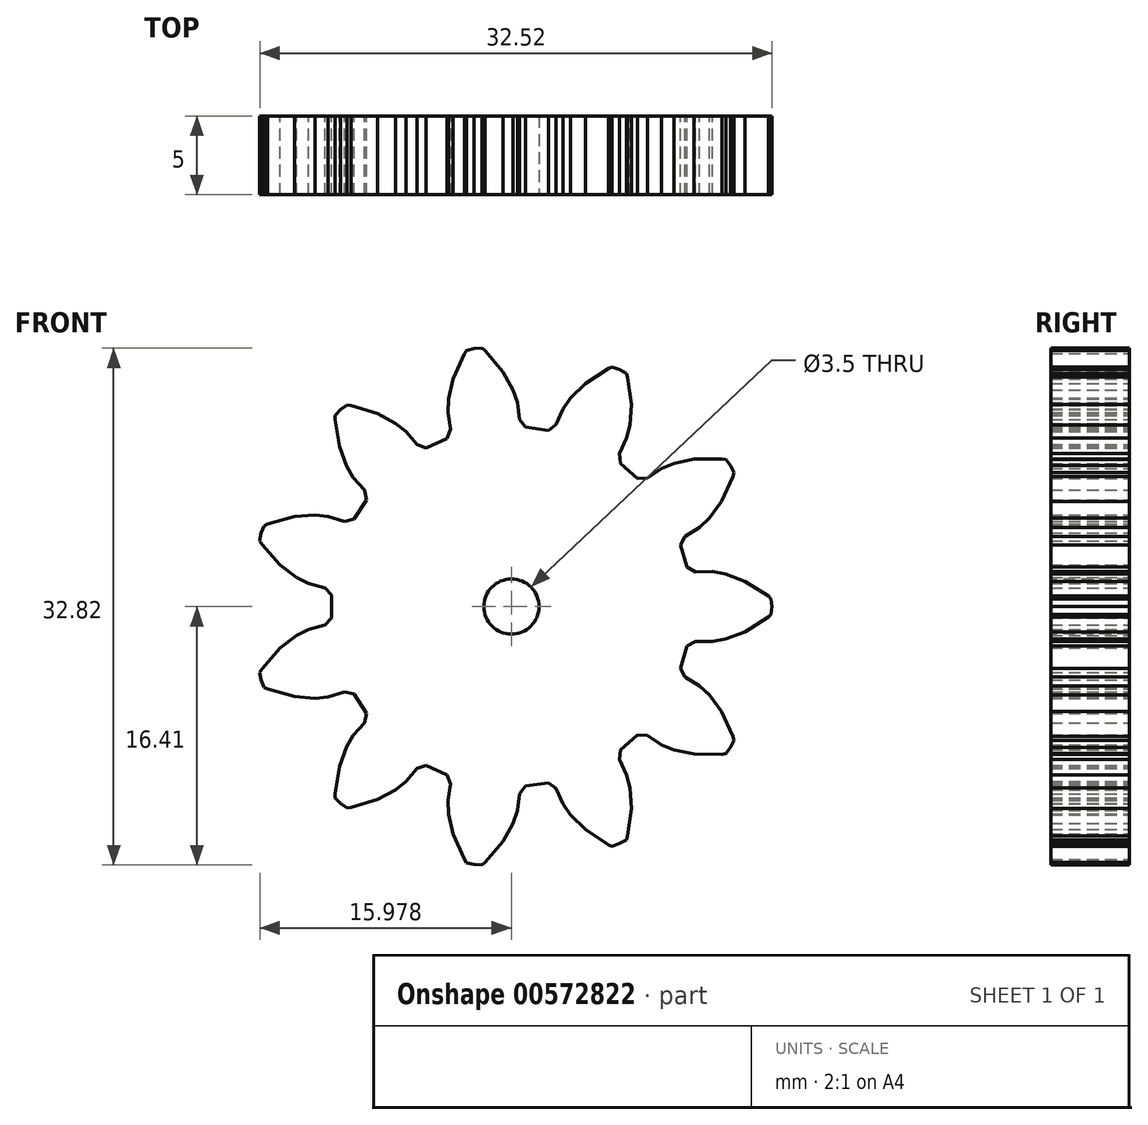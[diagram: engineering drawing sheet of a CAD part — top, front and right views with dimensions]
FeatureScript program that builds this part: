
annotation { "Feature Type Name" : "Feature", "Feature Type Description" : "" }
export const myFeature = defineFeature(function(context is Context, id is Id, definition is map)
    precondition{}
    {
        {
            var Q0;
            Q0=qCreatedBy(makeId("Front.planeOp"),FACE);
            var sketch = newSketch(context, id + "F0", { "sketchPlane" : qUnion([Q0])});
            skLineSegment(sketch, "E0", {"start": v(-15.98, 5.13) * mm, "end": v(-16.17, 4.66) * mm});
            skLineSegment(sketch, "E1", {"start": v(-16.17, 4.66) * mm, "end": v(-16.26, 4.17) * mm});
            skLineSegment(sketch, "E2", {"start": v(-16.26, 4.17) * mm, "end": v(-16.14, 3.96) * mm});
            skLineSegment(sketch, "E3", {"start": v(-16.14, 3.96) * mm, "end": v(-14.97, 2.64) * mm});
            skLineSegment(sketch, "E4", {"start": v(-14.97, 2.64) * mm, "end": v(-13.93, 1.85) * mm});
            skLineSegment(sketch, "E5", {"start": v(-13.93, 1.85) * mm, "end": v(-13.17, 1.47) * mm});
            skLineSegment(sketch, "E6", {"start": v(-13.17, 1.47) * mm, "end": v(-12.13, 1.18) * mm});
            skLineSegment(sketch, "E7", {"start": v(-12.13, 1.18) * mm, "end": v(-11.7, 0.73) * mm});
            skLineSegment(sketch, "E8", {"start": v(-11.7, 0.73) * mm, "end": v(-11.7, -0.73) * mm});
            skLineSegment(sketch, "E9", {"start": v(-11.7, -0.73) * mm, "end": v(-12.13, -1.18) * mm});
            skLineSegment(sketch, "E10", {"start": v(-12.13, -1.18) * mm, "end": v(-13.17, -1.47) * mm});
            skLineSegment(sketch, "E11", {"start": v(-13.17, -1.47) * mm, "end": v(-13.93, -1.85) * mm});
            skLineSegment(sketch, "E12", {"start": v(-13.93, -1.85) * mm, "end": v(-14.97, -2.64) * mm});
            skLineSegment(sketch, "E13", {"start": v(-14.97, -2.64) * mm, "end": v(-16.14, -3.96) * mm});
            skLineSegment(sketch, "E14", {"start": v(-16.14, -3.96) * mm, "end": v(-16.26, -4.17) * mm});
            skLineSegment(sketch, "E15", {"start": v(-16.26, -4.17) * mm, "end": v(-16.17, -4.66) * mm});
            skLineSegment(sketch, "E16", {"start": v(-16.17, -4.66) * mm, "end": v(-15.98, -5.13) * mm});
            skLineSegment(sketch, "E17", {"start": v(-15.98, -5.13) * mm, "end": v(-15.76, -5.24) * mm});
            skLineSegment(sketch, "E18", {"start": v(-15.76, -5.24) * mm, "end": v(-14.06, -5.71) * mm});
            skLineSegment(sketch, "E19", {"start": v(-14.06, -5.71) * mm, "end": v(-12.76, -5.82) * mm});
            skLineSegment(sketch, "E20", {"start": v(-12.76, -5.82) * mm, "end": v(-11.92, -5.73) * mm});
            skLineSegment(sketch, "E21", {"start": v(-11.92, -5.73) * mm, "end": v(-10.89, -5.41) * mm});
            skLineSegment(sketch, "E22", {"start": v(-10.89, -5.41) * mm, "end": v(-10.28, -5.55) * mm});
            skLineSegment(sketch, "E23", {"start": v(-10.28, -5.55) * mm, "end": v(-9.5, -6.78) * mm});
            skLineSegment(sketch, "E24", {"start": v(-9.5, -6.78) * mm, "end": v(-9.62, -7.4) * mm});
            skLineSegment(sketch, "E25", {"start": v(-9.62, -7.4) * mm, "end": v(-10.33, -8.2) * mm});
            skLineSegment(sketch, "E26", {"start": v(-10.33, -8.2) * mm, "end": v(-10.77, -8.93) * mm});
            skLineSegment(sketch, "E27", {"start": v(-10.77, -8.93) * mm, "end": v(-11.2, -10.16) * mm});
            skLineSegment(sketch, "E28", {"start": v(-11.2, -10.16) * mm, "end": v(-11.48, -11.9) * mm});
            skLineSegment(sketch, "E29", {"start": v(-11.48, -11.9) * mm, "end": v(-11.47, -12.15) * mm});
            skLineSegment(sketch, "E30", {"start": v(-11.47, -12.15) * mm, "end": v(-11.13, -12.5) * mm});
            skLineSegment(sketch, "E31", {"start": v(-11.13, -12.5) * mm, "end": v(-10.72, -12.8) * mm});
            skLineSegment(sketch, "E32", {"start": v(-10.72, -12.8) * mm, "end": v(-10.47, -12.77) * mm});
            skLineSegment(sketch, "E33", {"start": v(-10.47, -12.77) * mm, "end": v(-8.79, -12.25) * mm});
            skLineSegment(sketch, "E34", {"start": v(-8.79, -12.25) * mm, "end": v(-7.64, -11.64) * mm});
            skLineSegment(sketch, "E35", {"start": v(-7.64, -11.64) * mm, "end": v(-6.97, -11.1) * mm});
            skLineSegment(sketch, "E36", {"start": v(-6.97, -11.1) * mm, "end": v(-6.28, -10.29) * mm});
            skLineSegment(sketch, "E37", {"start": v(-6.28, -10.29) * mm, "end": v(-5.7, -10.07) * mm});
            skLineSegment(sketch, "E38", {"start": v(-5.7, -10.07) * mm, "end": v(-4.36, -10.68) * mm});
            skLineSegment(sketch, "E39", {"start": v(-4.36, -10.68) * mm, "end": v(-4.14, -11.26) * mm});
            skLineSegment(sketch, "E40", {"start": v(-4.14, -11.26) * mm, "end": v(-4.3, -12.33) * mm});
            skLineSegment(sketch, "E41", {"start": v(-4.3, -12.33) * mm, "end": v(-4.28, -13.18) * mm});
            skLineSegment(sketch, "E42", {"start": v(-4.28, -13.18) * mm, "end": v(-3.98, -14.45) * mm});
            skLineSegment(sketch, "E43", {"start": v(-3.98, -14.45) * mm, "end": v(-3.27, -16.06) * mm});
            skLineSegment(sketch, "E44", {"start": v(-3.27, -16.06) * mm, "end": v(-3.13, -16.27) * mm});
            skLineSegment(sketch, "E45", {"start": v(-3.13, -16.27) * mm, "end": v(-2.64, -16.38) * mm});
            skLineSegment(sketch, "E46", {"start": v(-2.64, -16.38) * mm, "end": v(-2.15, -16.4) * mm});
            skLineSegment(sketch, "E47", {"start": v(-2.15, -16.4) * mm, "end": v(-1.95, -16.25) * mm});
            skLineSegment(sketch, "E48", {"start": v(-1.95, -16.25) * mm, "end": v(-0.81, -14.9) * mm});
            skLineSegment(sketch, "E49", {"start": v(-0.81, -14.9) * mm, "end": v(-0.17, -13.77) * mm});
            skLineSegment(sketch, "E50", {"start": v(-0.17, -13.77) * mm, "end": v(0.1, -12.96) * mm});
            skLineSegment(sketch, "E51", {"start": v(0.1, -12.96) * mm, "end": v(0.23, -11.9) * mm});
            skLineSegment(sketch, "E52", {"start": v(0.23, -11.9) * mm, "end": v(0.61, -11.4) * mm});
            skLineSegment(sketch, "E53", {"start": v(0.61, -11.4) * mm, "end": v(2.06, -11.19) * mm});
            skLineSegment(sketch, "E54", {"start": v(2.06, -11.19) * mm, "end": v(2.56, -11.56) * mm});
            skLineSegment(sketch, "E55", {"start": v(2.56, -11.56) * mm, "end": v(3, -12.54) * mm});
            skLineSegment(sketch, "E56", {"start": v(3, -12.54) * mm, "end": v(3.48, -13.24) * mm});
            skLineSegment(sketch, "E57", {"start": v(3.48, -13.24) * mm, "end": v(4.41, -14.15) * mm});
            skLineSegment(sketch, "E58", {"start": v(4.41, -14.15) * mm, "end": v(5.88, -15.12) * mm});
            skLineSegment(sketch, "E59", {"start": v(5.88, -15.12) * mm, "end": v(6.12, -15.22) * mm});
            skLineSegment(sketch, "E60", {"start": v(6.12, -15.22) * mm, "end": v(6.59, -15.06) * mm});
            skLineSegment(sketch, "E61", {"start": v(6.59, -15.06) * mm, "end": v(7.02, -14.8) * mm});
            skLineSegment(sketch, "E62", {"start": v(7.02, -14.8) * mm, "end": v(7.1, -14.57) * mm});
            skLineSegment(sketch, "E63", {"start": v(7.1, -14.57) * mm, "end": v(7.33, -12.82) * mm});
            skLineSegment(sketch, "E64", {"start": v(7.33, -12.82) * mm, "end": v(7.25, -11.52) * mm});
            skLineSegment(sketch, "E65", {"start": v(7.25, -11.52) * mm, "end": v(7.04, -10.7) * mm});
            skLineSegment(sketch, "E66", {"start": v(7.04, -10.7) * mm, "end": v(6.58, -9.72) * mm});
            skLineSegment(sketch, "E67", {"start": v(6.58, -9.72) * mm, "end": v(6.63, -9.1) * mm});
            skLineSegment(sketch, "E68", {"start": v(6.63, -9.1) * mm, "end": v(7.74, -8.14) * mm});
            skLineSegment(sketch, "E69", {"start": v(7.74, -8.14) * mm, "end": v(8.36, -8.18) * mm});
            skLineSegment(sketch, "E70", {"start": v(8.36, -8.18) * mm, "end": v(9.26, -8.77) * mm});
            skLineSegment(sketch, "E71", {"start": v(9.26, -8.77) * mm, "end": v(10.04, -9.1) * mm});
            skLineSegment(sketch, "E72", {"start": v(10.04, -9.1) * mm, "end": v(11.32, -9.36) * mm});
            skLineSegment(sketch, "E73", {"start": v(11.32, -9.36) * mm, "end": v(13.08, -9.38) * mm});
            skLineSegment(sketch, "E74", {"start": v(13.08, -9.38) * mm, "end": v(13.33, -9.34) * mm});
            skLineSegment(sketch, "E75", {"start": v(13.33, -9.34) * mm, "end": v(13.64, -8.95) * mm});
            skLineSegment(sketch, "E76", {"start": v(13.64, -8.95) * mm, "end": v(13.86, -8.5) * mm});
            skLineSegment(sketch, "E77", {"start": v(13.86, -8.5) * mm, "end": v(13.8, -8.26) * mm});
            skLineSegment(sketch, "E78", {"start": v(13.8, -8.26) * mm, "end": v(13.05, -6.67) * mm});
            skLineSegment(sketch, "E79", {"start": v(13.05, -6.67) * mm, "end": v(12.28, -5.62) * mm});
            skLineSegment(sketch, "E80", {"start": v(12.28, -5.62) * mm, "end": v(11.66, -5.04) * mm});
            skLineSegment(sketch, "E81", {"start": v(11.66, -5.04) * mm, "end": v(10.75, -4.47) * mm});
            skLineSegment(sketch, "E82", {"start": v(10.75, -4.47) * mm, "end": v(10.45, -3.92) * mm});
            skLineSegment(sketch, "E83", {"start": v(10.45, -3.92) * mm, "end": v(10.86, -2.51) * mm});
            skLineSegment(sketch, "E84", {"start": v(10.86, -2.51) * mm, "end": v(11.4, -2.2) * mm});
            skLineSegment(sketch, "E85", {"start": v(11.4, -2.2) * mm, "end": v(12.49, -2.22) * mm});
            skLineSegment(sketch, "E86", {"start": v(12.49, -2.22) * mm, "end": v(13.32, -2.07) * mm});
            skLineSegment(sketch, "E87", {"start": v(13.32, -2.07) * mm, "end": v(14.54, -1.6) * mm});
            skLineSegment(sketch, "E88", {"start": v(14.54, -1.6) * mm, "end": v(16.03, -0.67) * mm});
            skLineSegment(sketch, "E89", {"start": v(16.03, -0.67) * mm, "end": v(16.22, -0.5) * mm});
            skLineSegment(sketch, "E90", {"start": v(16.22, -0.5) * mm, "end": v(16.26, 0) * mm});
            skLineSegment(sketch, "E91", {"start": v(16.26, 0) * mm, "end": v(16.22, 0.5) * mm});
            skLineSegment(sketch, "E92", {"start": v(16.22, 0.5) * mm, "end": v(16.03, 0.67) * mm});
            skLineSegment(sketch, "E93", {"start": v(16.03, 0.67) * mm, "end": v(14.54, 1.6) * mm});
            skLineSegment(sketch, "E94", {"start": v(14.54, 1.6) * mm, "end": v(13.32, 2.07) * mm});
            skLineSegment(sketch, "E95", {"start": v(13.32, 2.07) * mm, "end": v(12.49, 2.22) * mm});
            skLineSegment(sketch, "E96", {"start": v(12.49, 2.22) * mm, "end": v(11.4, 2.2) * mm});
            skLineSegment(sketch, "E97", {"start": v(11.4, 2.2) * mm, "end": v(10.86, 2.51) * mm});
            skLineSegment(sketch, "E98", {"start": v(10.86, 2.51) * mm, "end": v(10.45, 3.92) * mm});
            skLineSegment(sketch, "E99", {"start": v(10.45, 3.92) * mm, "end": v(10.75, 4.47) * mm});
            skLineSegment(sketch, "E100", {"start": v(10.75, 4.47) * mm, "end": v(11.66, 5.04) * mm});
            skLineSegment(sketch, "E101", {"start": v(11.66, 5.04) * mm, "end": v(12.28, 5.62) * mm});
            skLineSegment(sketch, "E102", {"start": v(12.28, 5.62) * mm, "end": v(13.05, 6.67) * mm});
            skLineSegment(sketch, "E103", {"start": v(13.05, 6.67) * mm, "end": v(13.8, 8.26) * mm});
            skLineSegment(sketch, "E104", {"start": v(13.8, 8.26) * mm, "end": v(13.86, 8.5) * mm});
            skLineSegment(sketch, "E105", {"start": v(13.86, 8.5) * mm, "end": v(13.64, 8.95) * mm});
            skLineSegment(sketch, "E106", {"start": v(13.64, 8.95) * mm, "end": v(13.33, 9.34) * mm});
            skLineSegment(sketch, "E107", {"start": v(13.33, 9.34) * mm, "end": v(13.08, 9.38) * mm});
            skLineSegment(sketch, "E108", {"start": v(13.08, 9.38) * mm, "end": v(11.32, 9.36) * mm});
            skLineSegment(sketch, "E109", {"start": v(11.32, 9.36) * mm, "end": v(10.04, 9.1) * mm});
            skLineSegment(sketch, "E110", {"start": v(10.04, 9.1) * mm, "end": v(9.26, 8.77) * mm});
            skLineSegment(sketch, "E111", {"start": v(9.26, 8.77) * mm, "end": v(8.36, 8.18) * mm});
            skLineSegment(sketch, "E112", {"start": v(8.36, 8.18) * mm, "end": v(7.74, 8.14) * mm});
            skLineSegment(sketch, "E113", {"start": v(7.74, 8.14) * mm, "end": v(6.63, 9.1) * mm});
            skLineSegment(sketch, "E114", {"start": v(6.63, 9.1) * mm, "end": v(6.58, 9.72) * mm});
            skLineSegment(sketch, "E115", {"start": v(6.58, 9.72) * mm, "end": v(7.04, 10.7) * mm});
            skLineSegment(sketch, "E116", {"start": v(7.04, 10.7) * mm, "end": v(7.25, 11.52) * mm});
            skLineSegment(sketch, "E117", {"start": v(7.25, 11.52) * mm, "end": v(7.33, 12.82) * mm});
            skLineSegment(sketch, "E118", {"start": v(7.33, 12.82) * mm, "end": v(7.1, 14.57) * mm});
            skLineSegment(sketch, "E119", {"start": v(7.1, 14.57) * mm, "end": v(7.02, 14.8) * mm});
            skLineSegment(sketch, "E120", {"start": v(7.02, 14.8) * mm, "end": v(6.59, 15.06) * mm});
            skLineSegment(sketch, "E121", {"start": v(6.59, 15.06) * mm, "end": v(6.12, 15.22) * mm});
            skLineSegment(sketch, "E122", {"start": v(6.12, 15.22) * mm, "end": v(5.88, 15.12) * mm});
            skLineSegment(sketch, "E123", {"start": v(5.88, 15.12) * mm, "end": v(4.41, 14.15) * mm});
            skLineSegment(sketch, "E124", {"start": v(4.41, 14.15) * mm, "end": v(3.48, 13.24) * mm});
            skLineSegment(sketch, "E125", {"start": v(3.48, 13.24) * mm, "end": v(3, 12.54) * mm});
            skLineSegment(sketch, "E126", {"start": v(3, 12.54) * mm, "end": v(2.56, 11.56) * mm});
            skLineSegment(sketch, "E127", {"start": v(2.56, 11.56) * mm, "end": v(2.06, 11.19) * mm});
            skLineSegment(sketch, "E128", {"start": v(2.06, 11.19) * mm, "end": v(0.61, 11.4) * mm});
            skLineSegment(sketch, "E129", {"start": v(0.61, 11.4) * mm, "end": v(0.23, 11.9) * mm});
            skLineSegment(sketch, "E130", {"start": v(0.23, 11.9) * mm, "end": v(0.1, 12.96) * mm});
            skLineSegment(sketch, "E131", {"start": v(0.1, 12.96) * mm, "end": v(-0.17, 13.77) * mm});
            skLineSegment(sketch, "E132", {"start": v(-0.17, 13.77) * mm, "end": v(-0.81, 14.9) * mm});
            skLineSegment(sketch, "E133", {"start": v(-0.81, 14.9) * mm, "end": v(-1.95, 16.25) * mm});
            skLineSegment(sketch, "E134", {"start": v(-1.95, 16.25) * mm, "end": v(-2.15, 16.4) * mm});
            skLineSegment(sketch, "E135", {"start": v(-2.15, 16.4) * mm, "end": v(-2.64, 16.38) * mm});
            skLineSegment(sketch, "E136", {"start": v(-2.64, 16.38) * mm, "end": v(-3.13, 16.27) * mm});
            skLineSegment(sketch, "E137", {"start": v(-3.13, 16.27) * mm, "end": v(-3.27, 16.06) * mm});
            skLineSegment(sketch, "E138", {"start": v(-3.27, 16.06) * mm, "end": v(-3.98, 14.45) * mm});
            skLineSegment(sketch, "E139", {"start": v(-3.98, 14.45) * mm, "end": v(-4.28, 13.18) * mm});
            skLineSegment(sketch, "E140", {"start": v(-4.28, 13.18) * mm, "end": v(-4.3, 12.33) * mm});
            skLineSegment(sketch, "E141", {"start": v(-4.3, 12.33) * mm, "end": v(-4.14, 11.26) * mm});
            skLineSegment(sketch, "E142", {"start": v(-4.14, 11.26) * mm, "end": v(-4.36, 10.68) * mm});
            skLineSegment(sketch, "E143", {"start": v(-4.36, 10.68) * mm, "end": v(-5.7, 10.07) * mm});
            skLineSegment(sketch, "E144", {"start": v(-5.7, 10.07) * mm, "end": v(-6.28, 10.29) * mm});
            skLineSegment(sketch, "E145", {"start": v(-6.28, 10.29) * mm, "end": v(-6.97, 11.1) * mm});
            skLineSegment(sketch, "E146", {"start": v(-6.97, 11.1) * mm, "end": v(-7.64, 11.64) * mm});
            skLineSegment(sketch, "E147", {"start": v(-7.64, 11.64) * mm, "end": v(-8.79, 12.25) * mm});
            skLineSegment(sketch, "E148", {"start": v(-8.79, 12.25) * mm, "end": v(-10.47, 12.77) * mm});
            skLineSegment(sketch, "E149", {"start": v(-10.47, 12.77) * mm, "end": v(-10.72, 12.8) * mm});
            skLineSegment(sketch, "E150", {"start": v(-10.72, 12.8) * mm, "end": v(-11.13, 12.5) * mm});
            skLineSegment(sketch, "E151", {"start": v(-11.13, 12.5) * mm, "end": v(-11.47, 12.15) * mm});
            skLineSegment(sketch, "E152", {"start": v(-11.47, 12.15) * mm, "end": v(-11.48, 11.9) * mm});
            skLineSegment(sketch, "E153", {"start": v(-11.48, 11.9) * mm, "end": v(-11.2, 10.16) * mm});
            skLineSegment(sketch, "E154", {"start": v(-11.2, 10.16) * mm, "end": v(-10.77, 8.93) * mm});
            skLineSegment(sketch, "E155", {"start": v(-10.77, 8.93) * mm, "end": v(-10.33, 8.2) * mm});
            skLineSegment(sketch, "E156", {"start": v(-10.33, 8.2) * mm, "end": v(-9.62, 7.4) * mm});
            skLineSegment(sketch, "E157", {"start": v(-9.62, 7.4) * mm, "end": v(-9.5, 6.78) * mm});
            skLineSegment(sketch, "E158", {"start": v(-9.5, 6.78) * mm, "end": v(-10.28, 5.55) * mm});
            skLineSegment(sketch, "E159", {"start": v(-10.28, 5.55) * mm, "end": v(-10.89, 5.41) * mm});
            skLineSegment(sketch, "E160", {"start": v(-10.89, 5.41) * mm, "end": v(-11.92, 5.73) * mm});
            skLineSegment(sketch, "E161", {"start": v(-11.92, 5.73) * mm, "end": v(-12.76, 5.82) * mm});
            skLineSegment(sketch, "E162", {"start": v(-12.76, 5.82) * mm, "end": v(-14.06, 5.71) * mm});
            skLineSegment(sketch, "E163", {"start": v(-14.06, 5.71) * mm, "end": v(-15.76, 5.24) * mm});
            skLineSegment(sketch, "E164", {"start": v(-15.76, 5.24) * mm, "end": v(-15.98, 5.13) * mm});
            skLineSegment(sketch, "E165", {"start": v(-1.01, 1.34) * mm, "end": v(-0.72, 1.46) * mm});
            skLineSegment(sketch, "E166", {"start": v(-0.72, 1.46) * mm, "end": v(-0.4, 1.52) * mm});
            skLineSegment(sketch, "E167", {"start": v(-0.4, 1.52) * mm, "end": v(-0.09, 1.51) * mm});
            skLineSegment(sketch, "E168", {"start": v(-0.09, 1.51) * mm, "end": v(0.22, 1.44) * mm});
            skLineSegment(sketch, "E169", {"start": v(0.22, 1.44) * mm, "end": v(0.51, 1.3) * mm});
            skLineSegment(sketch, "E170", {"start": v(0.51, 1.3) * mm, "end": v(0.76, 1.1) * mm});
            skLineSegment(sketch, "E171", {"start": v(0.76, 1.1) * mm, "end": v(0.97, 0.86) * mm});
            skLineSegment(sketch, "E172", {"start": v(0.97, 0.86) * mm, "end": v(1.12, 0.58) * mm});
            skLineSegment(sketch, "E173", {"start": v(1.12, 0.58) * mm, "end": v(1.21, 0.27) * mm});
            skLineSegment(sketch, "E174", {"start": v(1.21, 0.27) * mm, "end": v(1.24, -0.04) * mm});
            skLineSegment(sketch, "E175", {"start": v(1.24, -0.04) * mm, "end": v(1.2, -0.36) * mm});
            skLineSegment(sketch, "E176", {"start": v(1.2, -0.36) * mm, "end": v(1.09, -0.66) * mm});
            skLineSegment(sketch, "E177", {"start": v(1.09, -0.66) * mm, "end": v(0.92, -0.93) * mm});
            skLineSegment(sketch, "E178", {"start": v(0.92, -0.93) * mm, "end": v(0.7, -1.16) * mm});
            skLineSegment(sketch, "E179", {"start": v(0.7, -1.16) * mm, "end": v(0.44, -1.34) * mm});
            skLineSegment(sketch, "E180", {"start": v(0.44, -1.34) * mm, "end": v(0.14, -1.46) * mm});
            skLineSegment(sketch, "E181", {"start": v(0.14, -1.46) * mm, "end": v(-0.17, -1.52) * mm});
            skLineSegment(sketch, "E182", {"start": v(-0.17, -1.52) * mm, "end": v(-0.5, -1.51) * mm});
            skLineSegment(sketch, "E183", {"start": v(-0.5, -1.51) * mm, "end": v(-0.8, -1.44) * mm});
            skLineSegment(sketch, "E184", {"start": v(-0.8, -1.44) * mm, "end": v(-1.09, -1.3) * mm});
            skLineSegment(sketch, "E185", {"start": v(-1.09, -1.3) * mm, "end": v(-1.34, -1.1) * mm});
            skLineSegment(sketch, "E186", {"start": v(-1.34, -1.1) * mm, "end": v(-1.55, -0.86) * mm});
            skLineSegment(sketch, "E187", {"start": v(-1.55, -0.86) * mm, "end": v(-1.7, -0.58) * mm});
            skLineSegment(sketch, "E188", {"start": v(-1.7, -0.58) * mm, "end": v(-1.79, -0.27) * mm});
            skLineSegment(sketch, "E189", {"start": v(-1.79, -0.27) * mm, "end": v(-1.81, 0.04) * mm});
            skLineSegment(sketch, "E190", {"start": v(-1.81, 0.04) * mm, "end": v(-1.77, 0.36) * mm});
            skLineSegment(sketch, "E191", {"start": v(-1.77, 0.36) * mm, "end": v(-1.66, 0.66) * mm});
            skLineSegment(sketch, "E192", {"start": v(-1.66, 0.66) * mm, "end": v(-1.5, 0.93) * mm});
            skLineSegment(sketch, "E193", {"start": v(-1.5, 0.93) * mm, "end": v(-1.28, 1.16) * mm});
            skLineSegment(sketch, "E194", {"start": v(-1.28, 1.16) * mm, "end": v(-1.01, 1.34) * mm});
            skSolve(sketch);
        }
        {
            var Q0;
            Q0 = qSketchRegion(id + "F0", true);
            extrude(context, id + "F1", {"entities" : qUnion([Q0]), "depth" : 5 * mm, "offsetDistance" : 25 * mm});
        }
        {
            var Q0;
            Q0=makeQuery(id+"F1.opExtrude","CAP_FACE",FACE,{"disambiguationData":[OSD([sQuery(id+"F0.wireOp",EDGE,"E0"),sQuery(id+"F0.wireOp",EDGE,"E1"),sQuery(id+"F0.wireOp",EDGE,"E2"),sQuery(id+"F0.wireOp",EDGE,"E3"),sQuery(id+"F0.wireOp",EDGE,"E4"),sQuery(id+"F0.wireOp",EDGE,"E5"),sQuery(id+"F0.wireOp",EDGE,"E6"),sQuery(id+"F0.wireOp",EDGE,"E7"),sQuery(id+"F0.wireOp",EDGE,"E8"),sQuery(id+"F0.wireOp",EDGE,"E9"),sQuery(id+"F0.wireOp",EDGE,"E10"),sQuery(id+"F0.wireOp",EDGE,"E11"),sQuery(id+"F0.wireOp",EDGE,"E12"),sQuery(id+"F0.wireOp",EDGE,"E13"),sQuery(id+"F0.wireOp",EDGE,"E14"),sQuery(id+"F0.wireOp",EDGE,"E15"),sQuery(id+"F0.wireOp",EDGE,"E16"),sQuery(id+"F0.wireOp",EDGE,"E17"),sQuery(id+"F0.wireOp",EDGE,"E18"),sQuery(id+"F0.wireOp",EDGE,"E19"),sQuery(id+"F0.wireOp",EDGE,"E20"),sQuery(id+"F0.wireOp",EDGE,"E21"),sQuery(id+"F0.wireOp",EDGE,"E22"),sQuery(id+"F0.wireOp",EDGE,"E23"),sQuery(id+"F0.wireOp",EDGE,"E24"),sQuery(id+"F0.wireOp",EDGE,"E25"),sQuery(id+"F0.wireOp",EDGE,"E26"),sQuery(id+"F0.wireOp",EDGE,"E27"),sQuery(id+"F0.wireOp",EDGE,"E28"),sQuery(id+"F0.wireOp",EDGE,"E29"),sQuery(id+"F0.wireOp",EDGE,"E30"),sQuery(id+"F0.wireOp",EDGE,"E31"),sQuery(id+"F0.wireOp",EDGE,"E32"),sQuery(id+"F0.wireOp",EDGE,"E33"),sQuery(id+"F0.wireOp",EDGE,"E34"),sQuery(id+"F0.wireOp",EDGE,"E35"),sQuery(id+"F0.wireOp",EDGE,"E36"),sQuery(id+"F0.wireOp",EDGE,"E37"),sQuery(id+"F0.wireOp",EDGE,"E38"),sQuery(id+"F0.wireOp",EDGE,"E39"),sQuery(id+"F0.wireOp",EDGE,"E40"),sQuery(id+"F0.wireOp",EDGE,"E41"),sQuery(id+"F0.wireOp",EDGE,"E42"),sQuery(id+"F0.wireOp",EDGE,"E43"),sQuery(id+"F0.wireOp",EDGE,"E44"),sQuery(id+"F0.wireOp",EDGE,"E45"),sQuery(id+"F0.wireOp",EDGE,"E46"),sQuery(id+"F0.wireOp",EDGE,"E47"),sQuery(id+"F0.wireOp",EDGE,"E48"),sQuery(id+"F0.wireOp",EDGE,"E49"),sQuery(id+"F0.wireOp",EDGE,"E50"),sQuery(id+"F0.wireOp",EDGE,"E51"),sQuery(id+"F0.wireOp",EDGE,"E52"),sQuery(id+"F0.wireOp",EDGE,"E53"),sQuery(id+"F0.wireOp",EDGE,"E54"),sQuery(id+"F0.wireOp",EDGE,"E55"),sQuery(id+"F0.wireOp",EDGE,"E56"),sQuery(id+"F0.wireOp",EDGE,"E57"),sQuery(id+"F0.wireOp",EDGE,"E58"),sQuery(id+"F0.wireOp",EDGE,"E59"),sQuery(id+"F0.wireOp",EDGE,"E60"),sQuery(id+"F0.wireOp",EDGE,"E61"),sQuery(id+"F0.wireOp",EDGE,"E62"),sQuery(id+"F0.wireOp",EDGE,"E63"),sQuery(id+"F0.wireOp",EDGE,"E64"),sQuery(id+"F0.wireOp",EDGE,"E65"),sQuery(id+"F0.wireOp",EDGE,"E66"),sQuery(id+"F0.wireOp",EDGE,"E67"),sQuery(id+"F0.wireOp",EDGE,"E68"),sQuery(id+"F0.wireOp",EDGE,"E69"),sQuery(id+"F0.wireOp",EDGE,"E70"),sQuery(id+"F0.wireOp",EDGE,"E71"),sQuery(id+"F0.wireOp",EDGE,"E72"),sQuery(id+"F0.wireOp",EDGE,"E73"),sQuery(id+"F0.wireOp",EDGE,"E74"),sQuery(id+"F0.wireOp",EDGE,"E75"),sQuery(id+"F0.wireOp",EDGE,"E76"),sQuery(id+"F0.wireOp",EDGE,"E77"),sQuery(id+"F0.wireOp",EDGE,"E78"),sQuery(id+"F0.wireOp",EDGE,"E79"),sQuery(id+"F0.wireOp",EDGE,"E80"),sQuery(id+"F0.wireOp",EDGE,"E81"),sQuery(id+"F0.wireOp",EDGE,"E82"),sQuery(id+"F0.wireOp",EDGE,"E83"),sQuery(id+"F0.wireOp",EDGE,"E84"),sQuery(id+"F0.wireOp",EDGE,"E85"),sQuery(id+"F0.wireOp",EDGE,"E86"),sQuery(id+"F0.wireOp",EDGE,"E87"),sQuery(id+"F0.wireOp",EDGE,"E88"),sQuery(id+"F0.wireOp",EDGE,"E89"),sQuery(id+"F0.wireOp",EDGE,"E90"),sQuery(id+"F0.wireOp",EDGE,"E91"),sQuery(id+"F0.wireOp",EDGE,"E92"),sQuery(id+"F0.wireOp",EDGE,"E93"),sQuery(id+"F0.wireOp",EDGE,"E94"),sQuery(id+"F0.wireOp",EDGE,"E95"),sQuery(id+"F0.wireOp",EDGE,"E96"),sQuery(id+"F0.wireOp",EDGE,"E97"),sQuery(id+"F0.wireOp",EDGE,"E98"),sQuery(id+"F0.wireOp",EDGE,"E99"),sQuery(id+"F0.wireOp",EDGE,"E100"),sQuery(id+"F0.wireOp",EDGE,"E101"),sQuery(id+"F0.wireOp",EDGE,"E102"),sQuery(id+"F0.wireOp",EDGE,"E103"),sQuery(id+"F0.wireOp",EDGE,"E104"),sQuery(id+"F0.wireOp",EDGE,"E105"),sQuery(id+"F0.wireOp",EDGE,"E106"),sQuery(id+"F0.wireOp",EDGE,"E107"),sQuery(id+"F0.wireOp",EDGE,"E108"),sQuery(id+"F0.wireOp",EDGE,"E109"),sQuery(id+"F0.wireOp",EDGE,"E110"),sQuery(id+"F0.wireOp",EDGE,"E111"),sQuery(id+"F0.wireOp",EDGE,"E112"),sQuery(id+"F0.wireOp",EDGE,"E113"),sQuery(id+"F0.wireOp",EDGE,"E114"),sQuery(id+"F0.wireOp",EDGE,"E115"),sQuery(id+"F0.wireOp",EDGE,"E116"),sQuery(id+"F0.wireOp",EDGE,"E117"),sQuery(id+"F0.wireOp",EDGE,"E118"),sQuery(id+"F0.wireOp",EDGE,"E119"),sQuery(id+"F0.wireOp",EDGE,"E120"),sQuery(id+"F0.wireOp",EDGE,"E121"),sQuery(id+"F0.wireOp",EDGE,"E122"),sQuery(id+"F0.wireOp",EDGE,"E123"),sQuery(id+"F0.wireOp",EDGE,"E124"),sQuery(id+"F0.wireOp",EDGE,"E125"),sQuery(id+"F0.wireOp",EDGE,"E126"),sQuery(id+"F0.wireOp",EDGE,"E127"),sQuery(id+"F0.wireOp",EDGE,"E128"),sQuery(id+"F0.wireOp",EDGE,"E129"),sQuery(id+"F0.wireOp",EDGE,"E130"),sQuery(id+"F0.wireOp",EDGE,"E131"),sQuery(id+"F0.wireOp",EDGE,"E132"),sQuery(id+"F0.wireOp",EDGE,"E133"),sQuery(id+"F0.wireOp",EDGE,"E134"),sQuery(id+"F0.wireOp",EDGE,"E135"),sQuery(id+"F0.wireOp",EDGE,"E136"),sQuery(id+"F0.wireOp",EDGE,"E137"),sQuery(id+"F0.wireOp",EDGE,"E138"),sQuery(id+"F0.wireOp",EDGE,"E139"),sQuery(id+"F0.wireOp",EDGE,"E140"),sQuery(id+"F0.wireOp",EDGE,"E141"),sQuery(id+"F0.wireOp",EDGE,"E142"),sQuery(id+"F0.wireOp",EDGE,"E143"),sQuery(id+"F0.wireOp",EDGE,"E144"),sQuery(id+"F0.wireOp",EDGE,"E145"),sQuery(id+"F0.wireOp",EDGE,"E146"),sQuery(id+"F0.wireOp",EDGE,"E147"),sQuery(id+"F0.wireOp",EDGE,"E148"),sQuery(id+"F0.wireOp",EDGE,"E149"),sQuery(id+"F0.wireOp",EDGE,"E150"),sQuery(id+"F0.wireOp",EDGE,"E151"),sQuery(id+"F0.wireOp",EDGE,"E152"),sQuery(id+"F0.wireOp",EDGE,"E153"),sQuery(id+"F0.wireOp",EDGE,"E154"),sQuery(id+"F0.wireOp",EDGE,"E155"),sQuery(id+"F0.wireOp",EDGE,"E156"),sQuery(id+"F0.wireOp",EDGE,"E157"),sQuery(id+"F0.wireOp",EDGE,"E158"),sQuery(id+"F0.wireOp",EDGE,"E159"),sQuery(id+"F0.wireOp",EDGE,"E160"),sQuery(id+"F0.wireOp",EDGE,"E161"),sQuery(id+"F0.wireOp",EDGE,"E162"),sQuery(id+"F0.wireOp",EDGE,"E163"),sQuery(id+"F0.wireOp",EDGE,"E164"),sQuery(id+"F0.wireOp",EDGE,"E165"),sQuery(id+"F0.wireOp",EDGE,"E166"),sQuery(id+"F0.wireOp",EDGE,"E167"),sQuery(id+"F0.wireOp",EDGE,"E168"),sQuery(id+"F0.wireOp",EDGE,"E169"),sQuery(id+"F0.wireOp",EDGE,"E170"),sQuery(id+"F0.wireOp",EDGE,"E171"),sQuery(id+"F0.wireOp",EDGE,"E172"),sQuery(id+"F0.wireOp",EDGE,"E173"),sQuery(id+"F0.wireOp",EDGE,"E174"),sQuery(id+"F0.wireOp",EDGE,"E175"),sQuery(id+"F0.wireOp",EDGE,"E176"),sQuery(id+"F0.wireOp",EDGE,"E177"),sQuery(id+"F0.wireOp",EDGE,"E178"),sQuery(id+"F0.wireOp",EDGE,"E179"),sQuery(id+"F0.wireOp",EDGE,"E180"),sQuery(id+"F0.wireOp",EDGE,"E181"),sQuery(id+"F0.wireOp",EDGE,"E182"),sQuery(id+"F0.wireOp",EDGE,"E183"),sQuery(id+"F0.wireOp",EDGE,"E184"),sQuery(id+"F0.wireOp",EDGE,"E185"),sQuery(id+"F0.wireOp",EDGE,"E186"),sQuery(id+"F0.wireOp",EDGE,"E187"),sQuery(id+"F0.wireOp",EDGE,"E188"),sQuery(id+"F0.wireOp",EDGE,"E189"),sQuery(id+"F0.wireOp",EDGE,"E190"),sQuery(id+"F0.wireOp",EDGE,"E191"),sQuery(id+"F0.wireOp",EDGE,"E192"),sQuery(id+"F0.wireOp",EDGE,"E193"),sQuery(id+"F0.wireOp",EDGE,"E194")])],"isStart":false});
            var sketch = newSketch(context, id + "F2", { "sketchPlane" : qUnion([Q0])});
            skCircle(sketch, "E195", {"center": v(-0.28, 0) * mm, "radius": 1.75 * mm});
            skSolve(sketch);
        }
        {
            var Q0;
            Q0 = qSketchRegion(id + "F2", true);
            extrude(context, id + "F3", {"entities" : qUnion([Q0]), "operationType" : NewBodyOperationType.REMOVE, "oppositeDirection" : true, "depth" : 25 * mm, "offsetDistance" : 25 * mm});
        }
    });
